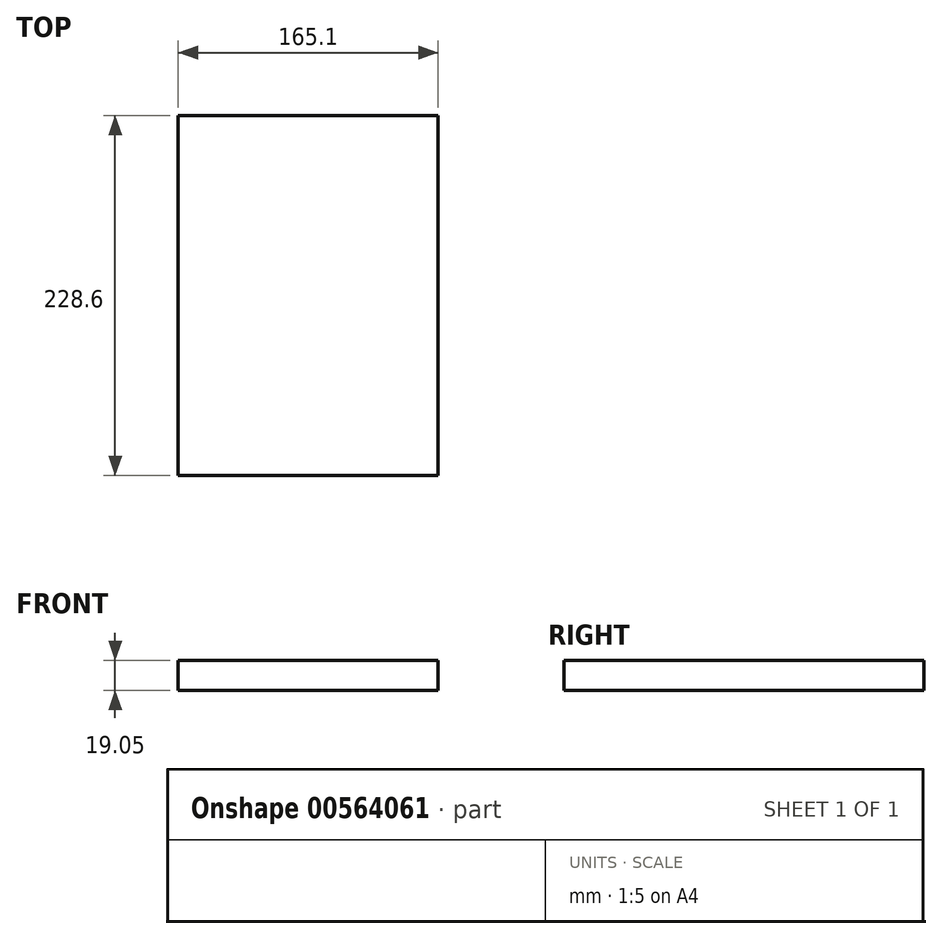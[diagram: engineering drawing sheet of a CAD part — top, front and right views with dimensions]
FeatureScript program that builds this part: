
annotation { "Feature Type Name" : "Feature", "Feature Type Description" : "" }
export const myFeature = defineFeature(function(context is Context, id is Id, definition is map)
    precondition{}
    {
        {
            var Q0;
            Q0=qCreatedBy(makeId("Top.planeOp"),FACE);
            var sketch = newSketch(context, id + "F0", { "sketchPlane" : qUnion([Q0])});
            skLineSegment(sketch, "E0.bottom", {"start": v(-82.55, 114.3) * mm, "end": v(82.55, 114.3) * mm});
            skLineSegment(sketch, "E0.top", {"start": v(-82.55, -114.3) * mm, "end": v(82.55, -114.3) * mm});
            skLineSegment(sketch, "E0.left", {"start": v(-82.55, 114.3) * mm, "end": v(-82.55, -114.3) * mm});
            skLineSegment(sketch, "E0.right", {"start": v(82.55, 114.3) * mm, "end": v(82.55, -114.3) * mm});
            skPoint(sketch, "E0.middle", {"position": v(0, 0) * mm});
            skSolve(sketch);
        }
        {
            var Q0;
            Q0 = qSketchRegion(id + "F0", true);
            extrude(context, id + "F1", {"entities" : qUnion([Q0]), "depth" : 19.05 * mm, "offsetDistance" : 25.4 * mm});
        }
    });
